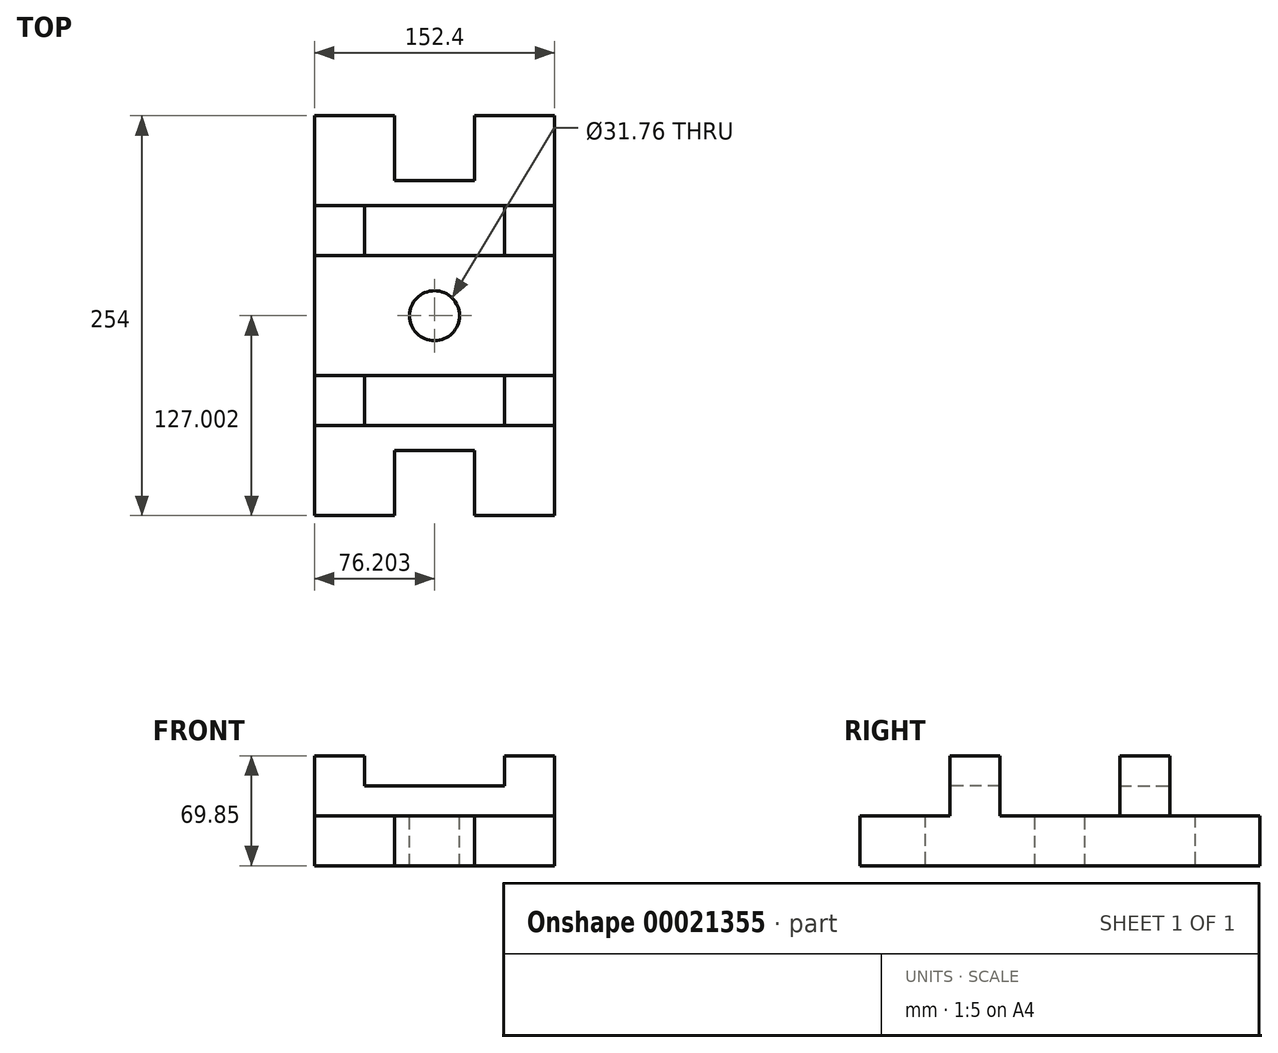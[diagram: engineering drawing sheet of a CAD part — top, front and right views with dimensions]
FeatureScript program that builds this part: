
annotation { "Feature Type Name" : "Feature", "Feature Type Description" : "" }
export const myFeature = defineFeature(function(context is Context, id is Id, definition is map)
    precondition{}
    {
        {
            var Q0;
            Q0=qCreatedBy(makeId("Top.planeOp"),FACE);
            var sketch = newSketch(context, id + "F0", { "sketchPlane" : qUnion([Q0])});
            skLineSegment(sketch, "E0", {"start": v(-84.98, 68.5) * mm, "end": v(67.42, 68.5) * mm});
            skLineSegment(sketch, "E1", {"start": v(-84.98, 68.5) * mm, "end": v(-84.98, -58.5) * mm});
            skLineSegment(sketch, "E2", {"start": v(-84.98, -58.5) * mm, "end": v(-34.18, -58.5) * mm});
            skLineSegment(sketch, "E3", {"start": v(-34.18, -58.5) * mm, "end": v(-34.18, -17.23) * mm});
            skLineSegment(sketch, "E4", {"start": v(-34.18, -17.23) * mm, "end": v(16.62, -17.23) * mm});
            skLineSegment(sketch, "E5", {"start": v(67.42, 68.5) * mm, "end": v(67.42, -58.5) * mm});
            skLineSegment(sketch, "E6", {"start": v(67.42, -58.5) * mm, "end": v(16.62, -58.5) * mm});
            skLineSegment(sketch, "E7", {"start": v(16.62, -58.5) * mm, "end": v(16.62, -17.23) * mm});
            skLineSegment(sketch, "E8.MirrorCS", {"start": v(-84.98, 68.5) * mm, "end": v(-84.98, 195.5) * mm});
            skLineSegment(sketch, "E9.MirrorCS", {"start": v(67.42, 195.5) * mm, "end": v(16.62, 195.5) * mm});
            skLineSegment(sketch, "E10.MirrorCS", {"start": v(-34.18, 154.22) * mm, "end": v(16.62, 154.22) * mm});
            skLineSegment(sketch, "E11.MirrorCS", {"start": v(67.42, 68.5) * mm, "end": v(67.42, 195.5) * mm});
            skLineSegment(sketch, "E12.MirrorCS", {"start": v(16.62, 195.5) * mm, "end": v(16.62, 154.22) * mm});
            skLineSegment(sketch, "E13.MirrorCS", {"start": v(-84.98, 195.5) * mm, "end": v(-34.18, 195.5) * mm});
            skLineSegment(sketch, "E14.MirrorCS", {"start": v(-34.18, 195.5) * mm, "end": v(-34.18, 154.22) * mm});
            skSolve(sketch);
        }
        {
            var Q0;
            Q0=makeQuery(id+"F0.imprint","IMPRINT",FACE,{"disambiguationData":[TD([[makeQuery(id+"F0.imprint","IMPRINT",EDGE,{"derivedFrom":sQuery(id+"F0.wireOp",EDGE,"E0")}),-1.0]])]});
            extrude(context, id + "F1", {"entities" : qUnion([Q0]), "depth" : 31.75 * mm});
        }
        {
            var Q0;
            Q0=makeQuery(id+"F0.imprint","IMPRINT",FACE,{"disambiguationData":[TD([[makeQuery(id+"F0.imprint","IMPRINT",EDGE,{"derivedFrom":sQuery(id+"F0.wireOp",EDGE,"E0")}),1.0]])]});
            extrude(context, id + "F2", {"entities" : qUnion([Q0]), "operationType" : NewBodyOperationType.ADD, "depth" : 31.75 * mm});
        }
        {
            var Q0;
            Q0=makeQuery(id+"F2.boolean.opBoolean","MERGE",FACE,{"derivedFrom":[makeQuery(id+"F1.opExtrude","SWEPT_FACE",FACE,{"disambiguationData":[OSD([sQuery(id+"F0.wireOp",EDGE,"E5")])]}),makeQuery(id+"F2.opExtrude","SWEPT_FACE",FACE,{"disambiguationData":[OSD([sQuery(id+"F0.wireOp",EDGE,"E11.MirrorCS")])]})]});
            var sketch = newSketch(context, id + "F3", { "sketchPlane" : qUnion([Q0])});
            skLineSegment(sketch, "E15", {"start": v(-1.36, 31.75) * mm, "end": v(-1.36, 69.85) * mm});
            skLineSegment(sketch, "E16", {"start": v(30.4, 31.75) * mm, "end": v(30.4, 69.85) * mm});
            skLineSegment(sketch, "E17", {"start": v(-1.36, 69.85) * mm, "end": v(30.4, 69.85) * mm});
            skLineSegment(sketch, "E18", {"start": v(-58.5, 31.75) * mm, "end": v(-1.36, 31.75) * mm});
            skLineSegment(sketch, "E19", {"start": v(106.6, 69.85) * mm, "end": v(138.34, 69.85) * mm});
            skLineSegment(sketch, "E20", {"start": v(138.34, 69.85) * mm, "end": v(138.34, 31.75) * mm});
            skLineSegment(sketch, "E21", {"start": v(138.34, 31.75) * mm, "end": v(195.5, 31.75) * mm});
            skLineSegment(sketch, "E22", {"start": v(106.6, 69.85) * mm, "end": v(106.6, 31.75) * mm});
            skSolve(sketch);
        }
        {
            var Q0;
            {var subQ2=sQuery(id+"F3.wireOp",EDGE,"E15");Q0=makeQuery(id+"F3.imprint","IMPRINT",FACE,{"disambiguationData":[TD([[makeQuery(id+"F3.imprint","IMPRINT",EDGE,{"derivedFrom":subQ2}),-1.0]])]});}
            extrude(context, id + "F4", {"entities" : qUnion([Q0]), "operationType" : NewBodyOperationType.ADD, "oppositeDirection" : true, "depth" : 152.4 * mm});
        }
        {
            var Q0;
            Q0=makeQuery(id+"F4.opExtrude","SWEPT_FACE",FACE,{"disambiguationData":[OSD([sQuery(id+"F3.wireOp",EDGE,"E15")])]});
            var sketch = newSketch(context, id + "F5", { "sketchPlane" : qUnion([Q0])});
            skLineSegment(sketch, "E23", {"start": v(-53.23, 69.85) * mm, "end": v(-53.23, 50.8) * mm});
            skLineSegment(sketch, "E24", {"start": v(-53.23, 50.8) * mm, "end": v(35.67, 50.8) * mm});
            skLineSegment(sketch, "E25", {"start": v(35.67, 50.8) * mm, "end": v(35.67, 69.85) * mm});
            skLineSegment(sketch, "E26", {"start": v(-53.23, 69.85) * mm, "end": v(-84.98, 69.85) * mm});
            skLineSegment(sketch, "E27", {"start": v(35.67, 69.85) * mm, "end": v(67.42, 69.85) * mm});
            skLineSegment(sketch, "E28", {"start": v(-11.8, 69.85) * mm, "end": v(-11.8, 50.8) * mm});
            skSolve(sketch);
        }
        {
            var Q0;
            {var subQ2=sQuery(id+"F5.wireOp",EDGE,"E23");Q0=makeQuery(id+"F5.imprint","IMPRINT",FACE,{"disambiguationData":[TD([[makeQuery(id+"F5.imprint","IMPRINT",EDGE,{"derivedFrom":subQ2}),1.0]])]});}
            var Q1;
            {var subQ2=sQuery(id+"F5.wireOp",EDGE,"E25");Q1=makeQuery(id+"F5.imprint","IMPRINT",FACE,{"disambiguationData":[TD([[makeQuery(id+"F5.imprint","IMPRINT",EDGE,{"derivedFrom":subQ2}),1.0]])]});}
            extrude(context, id + "F6", {"entities" : qUnion([Q0, Q1]), "operationType" : NewBodyOperationType.REMOVE, "oppositeDirection" : true, "depth" : 78.24 * mm});
        }
        {
            var Q0;
            Q0=makeQuery(id+"F3.imprint","IMPRINT",FACE,{"disambiguationData":[TD([[makeQuery(id+"F3.imprint","IMPRINT",EDGE,{"derivedFrom":sQuery(id+"F3.wireOp",EDGE,"E19")}),-1.0]])]});
            extrude(context, id + "F7", {"entities" : qUnion([Q0]), "oppositeDirection" : true, "depth" : 152.4 * mm});
        }
        {
            var Q0;
            Q0=makeQuery(id+"F7.opExtrude","SWEPT_FACE",FACE,{"disambiguationData":[OSD([sQuery(id+"F3.wireOp",EDGE,"E20")])]});
            var sketch = newSketch(context, id + "F8", { "sketchPlane" : qUnion([Q0])});
            skLineSegment(sketch, "E29", {"start": v(-35.67, 69.85) * mm, "end": v(-35.67, 50.8) * mm});
            skLineSegment(sketch, "E30", {"start": v(-35.67, 50.8) * mm, "end": v(53.23, 50.8) * mm});
            skLineSegment(sketch, "E31", {"start": v(53.23, 50.8) * mm, "end": v(53.23, 69.85) * mm});
            skLineSegment(sketch, "E32", {"start": v(-67.42, 69.85) * mm, "end": v(-35.67, 69.85) * mm});
            skLineSegment(sketch, "E33", {"start": v(53.23, 69.85) * mm, "end": v(84.98, 69.85) * mm});
            skLineSegment(sketch, "E34", {"start": v(8.78, 69.85) * mm, "end": v(8.78, 50.8) * mm});
            skSolve(sketch);
        }
        {
            var Q0;
            {var subQ2=sQuery(id+"F8.wireOp",EDGE,"E29");Q0=makeQuery(id+"F8.imprint","IMPRINT",FACE,{"disambiguationData":[TD([[makeQuery(id+"F8.imprint","IMPRINT",EDGE,{"derivedFrom":subQ2}),1.0]])]});}
            var Q1;
            {var subQ2=sQuery(id+"F8.wireOp",EDGE,"E31");Q1=makeQuery(id+"F8.imprint","IMPRINT",FACE,{"disambiguationData":[TD([[makeQuery(id+"F8.imprint","IMPRINT",EDGE,{"derivedFrom":subQ2}),1.0]])]});}
            extrude(context, id + "F9", {"entities" : qUnion([Q0, Q1]), "operationType" : NewBodyOperationType.REMOVE, "oppositeDirection" : true, "depth" : 54.92 * mm});
        }
        {
            var Q0;
            {var subQ0=sQuery(id+"F0.wireOp",EDGE,"E0");var subQ1=sQuery(id+"F0.wireOp",EDGE,"E1");var subQ2=sQuery(id+"F0.wireOp",EDGE,"E5");var subQ3=sQuery(id+"F0.wireOp",EDGE,"E8.MirrorCS");var subQ4=sQuery(id+"F0.wireOp",EDGE,"E9.MirrorCS");var subQ5=sQuery(id+"F0.wireOp",EDGE,"E10.MirrorCS");var subQ6=sQuery(id+"F0.wireOp",EDGE,"E11.MirrorCS");var subQ7=sQuery(id+"F0.wireOp",EDGE,"E12.MirrorCS");var subQ8=sQuery(id+"F0.wireOp",EDGE,"E13.MirrorCS");var subQ9=sQuery(id+"F0.wireOp",EDGE,"E14.MirrorCS");Q0=makeQuery(id+"F4.boolean.opBoolean","SPLIT",FACE,{"disambiguationData":[TD([makeQuery(id+"F2.opExtrude","SWEPT_FACE",FACE,{"disambiguationData":[OSD([subQ4])]})])],"derivedFrom":makeQuery(id+"F2.boolean.opBoolean","MERGE",FACE,{"derivedFrom":[makeQuery(id+"F1.opExtrude","CAP_FACE",FACE,{"disambiguationData":[OSD([subQ0,subQ1,sQuery(id+"F0.wireOp",EDGE,"E2"),sQuery(id+"F0.wireOp",EDGE,"E3"),sQuery(id+"F0.wireOp",EDGE,"E4"),subQ2,sQuery(id+"F0.wireOp",EDGE,"E6"),sQuery(id+"F0.wireOp",EDGE,"E7")])],"isStart":false}),makeQuery(id+"F2.opExtrude","CAP_FACE",FACE,{"disambiguationData":[OSD([subQ0,subQ3,subQ4,subQ5,subQ6,subQ7,subQ8,subQ9])],"isStart":false})]})});}
            var sketch = newSketch(context, id + "F10", { "sketchPlane" : qUnion([Q0])});
            skCircle(sketch, "E35", {"center": v(-8.78, 68.5) * mm, "radius": 15.88 * mm});
            skSolve(sketch);
        }
        {
            var Q0;
            Q0=makeQuery(id+"F10.imprint","IMPRINT",FACE,{"disambiguationData":[TD([[makeQuery(id+"F10.imprint","IMPRINT",EDGE,{"derivedFrom":sQuery(id+"F10.wireOp",EDGE,"E35")}),1.0]])]});
            extrude(context, id + "F11", {"entities" : qUnion([Q0]), "operationType" : NewBodyOperationType.REMOVE, "oppositeDirection" : true, "depth" : 294.58 * mm});
        }
    });
